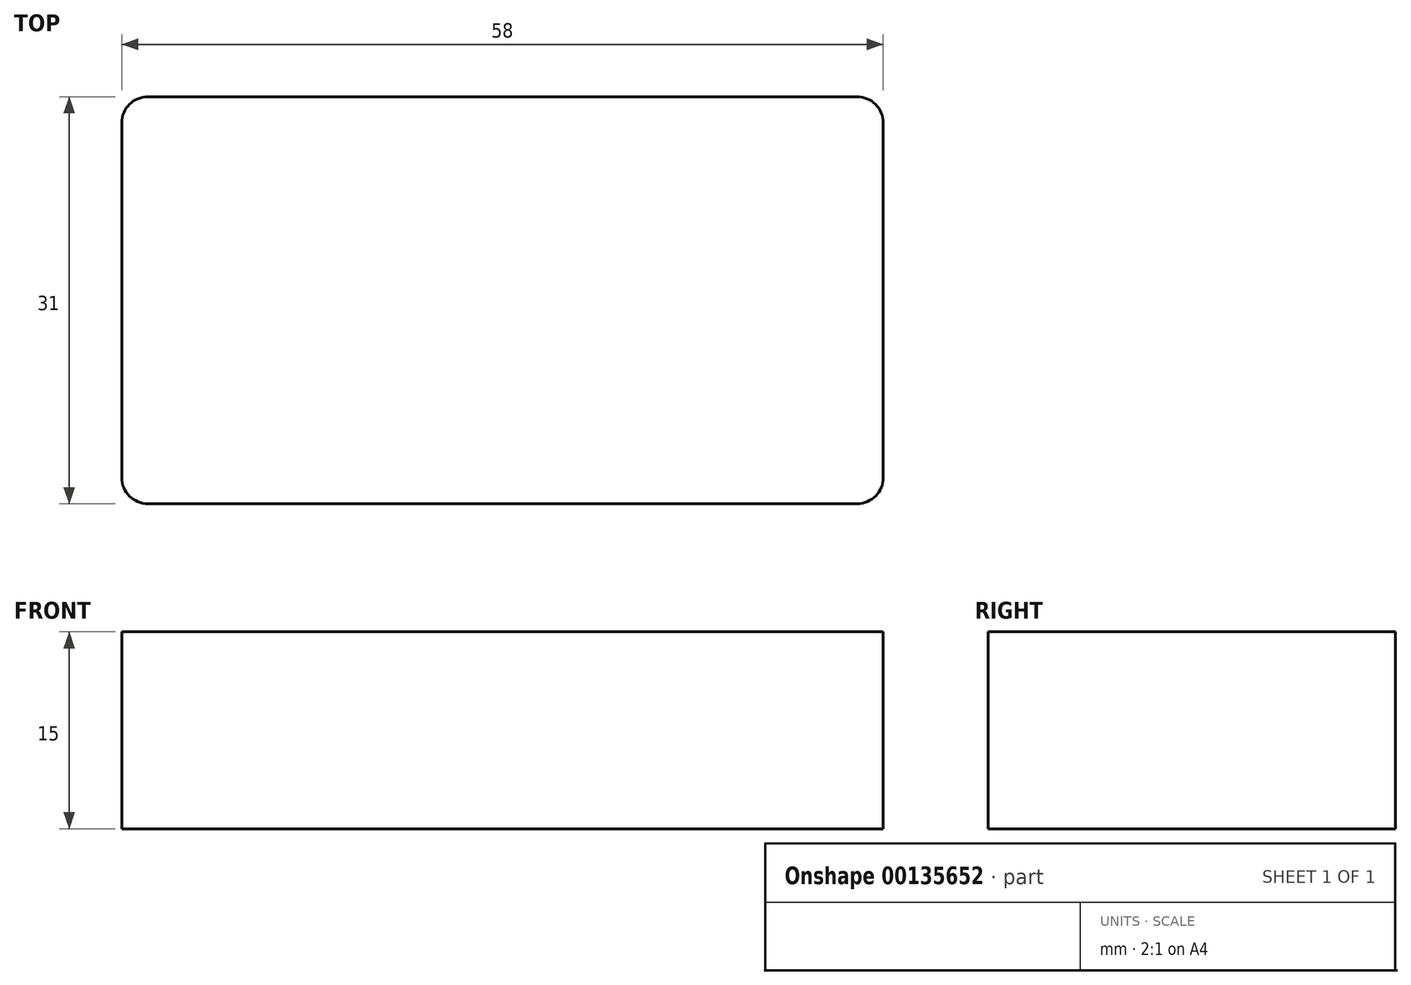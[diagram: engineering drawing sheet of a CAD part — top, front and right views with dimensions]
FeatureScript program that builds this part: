
annotation { "Feature Type Name" : "Feature", "Feature Type Description" : "" }
export const myFeature = defineFeature(function(context is Context, id is Id, definition is map)
    precondition{}
    {
        {
            var Q0;
            Q0=qCreatedBy(makeId("Top.planeOp"),FACE);
            var sketch = newSketch(context, id + "F0", { "sketchPlane" : qUnion([Q0])});
            skLineSegment(sketch, "E0.bottom", {"start": v(-29, -15.5) * mm, "end": v(29, -15.5) * mm});
            skLineSegment(sketch, "E0.top", {"start": v(-29, 15.5) * mm, "end": v(29, 15.5) * mm});
            skLineSegment(sketch, "E0.left", {"start": v(-29, -15.5) * mm, "end": v(-29, 15.5) * mm});
            skLineSegment(sketch, "E0.right", {"start": v(29, -15.5) * mm, "end": v(29, 15.5) * mm});
            skPoint(sketch, "E0.middle", {"position": v(0, 0) * mm});
            skSolve(sketch);
        }
        {
            var Q0;
            Q0=makeQuery(id+"F0.imprint","IMPRINT",FACE,{"disambiguationData":[TD([[makeQuery(id+"F0.imprint","IMPRINT",EDGE,{"derivedFrom":sQuery(id+"F0.wireOp",EDGE,"E0.bottom")}),1.0]])]});
            extrude(context, id + "F1", {"entities" : qUnion([Q0]), "depth" : 15 * mm});
        }
        {
            var Q0;
            Q0=makeQuery(id+"F1.opExtrude","SWEPT_EDGE",EDGE,{"disambiguationData":[OSD([sQuery(id+"F0.wireOp",EDGE,"E0.top"),sQuery(id+"F0.wireOp",EDGE,"E0.left")])]});
            var Q1;
            Q1=makeQuery(id+"F1.opExtrude","SWEPT_EDGE",EDGE,{"disambiguationData":[OSD([sQuery(id+"F0.wireOp",EDGE,"E0.bottom"),sQuery(id+"F0.wireOp",EDGE,"E0.left")])]});
            var Q2;
            Q2=makeQuery(id+"F1.opExtrude","SWEPT_EDGE",EDGE,{"disambiguationData":[OSD([sQuery(id+"F0.wireOp",EDGE,"E0.top"),sQuery(id+"F0.wireOp",EDGE,"E0.right")])]});
            var Q3;
            Q3=makeQuery(id+"F1.opExtrude","SWEPT_EDGE",EDGE,{"disambiguationData":[OSD([sQuery(id+"F0.wireOp",EDGE,"E0.bottom"),sQuery(id+"F0.wireOp",EDGE,"E0.right")])]});
            fillet(context, id + "F2", {"entities" : qUnion([Q0, Q1, Q2, Q3]), "radius" : 2 * mm, "tangentPropagation" : true, "allowEdgeOverflow" : false});
        }
    });
